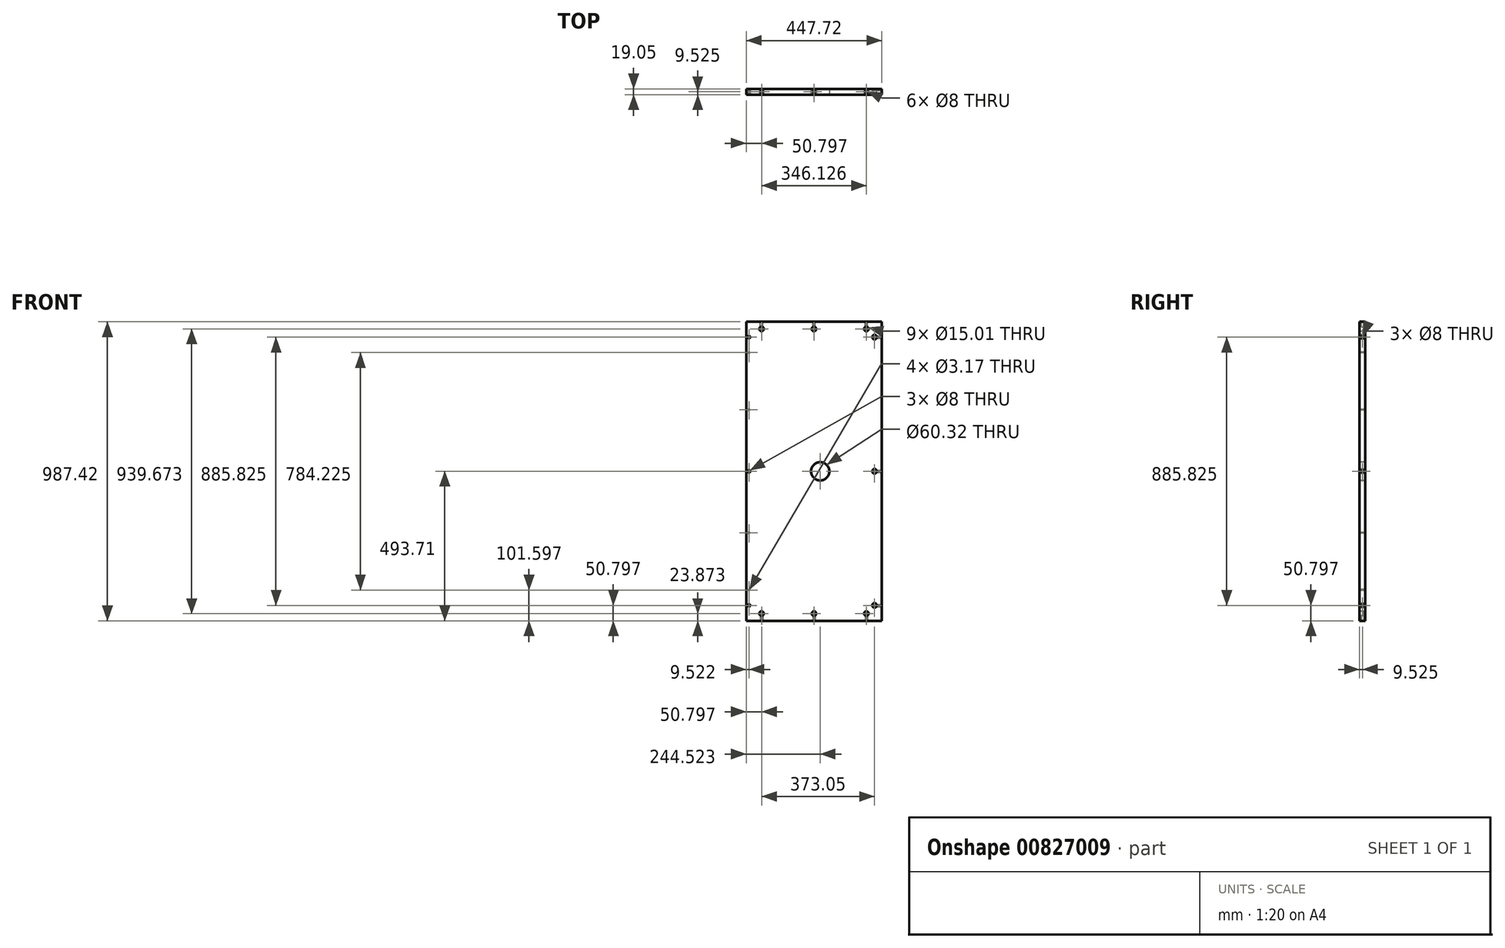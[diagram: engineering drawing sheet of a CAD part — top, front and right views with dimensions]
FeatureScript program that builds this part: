
annotation { "Feature Type Name" : "Feature", "Feature Type Description" : "" }
export const myFeature = defineFeature(function(context is Context, id is Id, definition is map)
    precondition{}
    {
        {
            var Q0;
            Q0=qCreatedBy(makeId("Front.planeOp"),FACE);
            var sketch = newSketch(context, id + "F0", { "sketchPlane" : qUnion([Q0])});
            skLineSegment(sketch, "E0.bottom", {"start": v(223.86, 493.71) * mm, "end": v(-223.86, 493.71) * mm});
            skLineSegment(sketch, "E0.top", {"start": v(223.86, -493.71) * mm, "end": v(-223.86, -493.71) * mm});
            skLineSegment(sketch, "E0.left", {"start": v(223.86, 493.71) * mm, "end": v(223.86, -493.71) * mm});
            skLineSegment(sketch, "E0.right", {"start": v(-223.86, 493.71) * mm, "end": v(-223.86, -493.71) * mm});
            skPoint(sketch, "E0.middle", {"position": v(0, 0) * mm});
            skSolve(sketch);
        }
        {
            var Q0;
            Q0=makeQuery(id+"F0.imprint","IMPRINT",FACE,{"disambiguationData":[TD([[makeQuery(id+"F0.imprint","IMPRINT",EDGE,{"derivedFrom":sQuery(id+"F0.wireOp",EDGE,"E0.bottom")}),1.0]])]});
            extrude(context, id + "F1", {"entities" : qUnion([Q0]), "depth" : 19.05 * mm, "offsetDistance" : 25.4 * mm});
        }
        {
            var Q0;
            Q0=makeQuery(id+"F1.opExtrude","CAP_FACE",FACE,{"disambiguationData":[OSD([sQuery(id+"F0.wireOp",EDGE,"E0.bottom"),sQuery(id+"F0.wireOp",EDGE,"E0.top"),sQuery(id+"F0.wireOp",EDGE,"E0.left"),sQuery(id+"F0.wireOp",EDGE,"E0.right")])],"isStart":false});
            var sketch = newSketch(context, id + "F2", { "sketchPlane" : qUnion([Q0])});
            skLineSegment(sketch, "E1", {"start": v(-223.86, 493.71) * mm, "end": v(-214.34, 493.71) * mm});
            skLineSegment(sketch, "E2", {"start": v(-214.34, 493.71) * mm, "end": v(-214.34, 442.91) * mm});
            skLineSegment(sketch, "E3", {"start": v(-223.86, -493.71) * mm, "end": v(-214.34, -493.71) * mm});
            skLineSegment(sketch, "E4", {"start": v(-214.34, -493.71) * mm, "end": v(-214.34, -442.91) * mm});
            skLineSegment(sketch, "E5", {"start": v(-223.86, 0) * mm, "end": v(-214.34, 0) * mm});
            skPoint(sketch, "E6", {"position": v(-214.34, 442.91) * mm});
            skPoint(sketch, "E7", {"position": v(-214.34, 0) * mm});
            skPoint(sketch, "E8", {"position": v(-214.34, -442.91) * mm});
            skLineSegment(sketch, "E9", {"start": v(-214.34, 442.91) * mm, "end": v(-214.34, 392.11) * mm});
            skLineSegment(sketch, "E10", {"start": v(-214.34, -442.91) * mm, "end": v(-214.34, -392.11) * mm});
            skLineSegment(sketch, "E11", {"start": v(-214.34, 0) * mm, "end": v(-214.34, -203.2) * mm});
            skLineSegment(sketch, "E12", {"start": v(-214.34, 0) * mm, "end": v(-214.34, 203.2) * mm});
            skSolve(sketch);
        }
        {
            var Q0;
            Q0=sQuery(id+"F2.wireOp",VERTEX,"E6");
            var Q1;
            Q1=sQuery(id+"F2.wireOp",VERTEX,"E7");
            var Q2;
            Q2=sQuery(id+"F2.wireOp",VERTEX,"E8");
            var Q3;
            Q3=makeQuery(id+"F1.opExtrude","SWEPT_BODY",BODY,{"disambiguationData":[OSD([sQuery(id+"F0.wireOp",EDGE,"E0.bottom"),sQuery(id+"F0.wireOp",EDGE,"E0.top"),sQuery(id+"F0.wireOp",EDGE,"E0.left"),sQuery(id+"F0.wireOp",EDGE,"E0.right")])]});
            hole(context, id + "F3", {"style" : HoleStyle.SIMPLE, "endStyle" : HoleEndStyle.BLIND, "holeDiameter" : 8 * mm, "majorDiameter" : 6.35 * mm, "holeDepth" : 25.4 * mm, "isTappedThrough" : true, "tappedDepth" : 12.7 * mm, "tapClearance" : 3, "startFromSketch" : true, "locations" : qUnion([Q0, Q1, Q2]), "scope" : qUnion([Q3])});
        }
        {
            var Q0;
            Q0=makeQuery(id+"F1.opExtrude","CAP_FACE",FACE,{"disambiguationData":[OSD([sQuery(id+"F0.wireOp",EDGE,"E0.bottom"),sQuery(id+"F0.wireOp",EDGE,"E0.top"),sQuery(id+"F0.wireOp",EDGE,"E0.left"),sQuery(id+"F0.wireOp",EDGE,"E0.right")])],"isStart":false});
            var sketch = newSketch(context, id + "F4", { "sketchPlane" : qUnion([Q0])});
            skLineSegment(sketch, "E13", {"start": v(-223.86, 493.71) * mm, "end": v(-173.06, 493.71) * mm});
            skLineSegment(sketch, "E14", {"start": v(-173.06, 493.71) * mm, "end": v(-173.06, 469.84) * mm});
            skLineSegment(sketch, "E15", {"start": v(223.86, 493.71) * mm, "end": v(173.06, 493.71) * mm});
            skLineSegment(sketch, "E16", {"start": v(173.06, 493.71) * mm, "end": v(173.06, 469.84) * mm});
            skLineSegment(sketch, "E17", {"start": v(0, 493.71) * mm, "end": v(0, 469.84) * mm});
            skLineSegment(sketch, "E18", {"start": v(-223.86, -493.71) * mm, "end": v(-173.06, -493.71) * mm});
            skLineSegment(sketch, "E19", {"start": v(-173.06, -493.71) * mm, "end": v(-173.06, -469.84) * mm});
            skLineSegment(sketch, "E20", {"start": v(223.86, -493.71) * mm, "end": v(173.06, -493.71) * mm});
            skLineSegment(sketch, "E21", {"start": v(173.06, -493.71) * mm, "end": v(173.06, -469.84) * mm});
            skLineSegment(sketch, "E22", {"start": v(0, -493.71) * mm, "end": v(0, -469.84) * mm});
            skLineSegment(sketch, "E23", {"start": v(223.86, 493.71) * mm, "end": v(223.86, 442.91) * mm});
            skLineSegment(sketch, "E24", {"start": v(223.86, 442.91) * mm, "end": v(199.99, 442.91) * mm});
            skLineSegment(sketch, "E25", {"start": v(223.86, -493.71) * mm, "end": v(223.86, -442.91) * mm});
            skLineSegment(sketch, "E26", {"start": v(223.86, -442.91) * mm, "end": v(199.99, -442.91) * mm});
            skLineSegment(sketch, "E27", {"start": v(223.86, 0) * mm, "end": v(199.99, 0) * mm});
            skLineSegment(sketch, "E28", {"start": v(223.86, 0) * mm, "end": v(20.66, 0) * mm});
            skCircle(sketch, "E29", {"center": v(20.66, 0) * mm, "radius": 30.16 * mm});
            skSolve(sketch);
        }
        {
            var Q0;
            Q0=makeQuery(id+"F4.imprint","IMPRINT",FACE,{"disambiguationData":[TD([[makeQuery(id+"F4.imprint","IMPRINT",EDGE,{"derivedFrom":sQuery(id+"F4.wireOp",EDGE,"E29")}),1.0]])]});
            extrude(context, id + "F5", {"entities" : qUnion([Q0]), "operationType" : NewBodyOperationType.REMOVE, "oppositeDirection" : true, "depth" : 25.4 * mm, "offsetDistance" : 25.4 * mm});
        }
        {
            var Q0;
            Q0=sQuery(id+"F4.wireOp",VERTEX,"E14.end");
            var Q1;
            Q1=sQuery(id+"F4.wireOp",VERTEX,"E17.end");
            var Q2;
            Q2=sQuery(id+"F4.wireOp",VERTEX,"E16.end");
            var Q3;
            Q3=sQuery(id+"F4.wireOp",VERTEX,"E24.end");
            var Q4;
            Q4=sQuery(id+"F4.wireOp",VERTEX,"E27.end");
            var Q5;
            Q5=sQuery(id+"F4.wireOp",VERTEX,"E26.end");
            var Q6;
            Q6=sQuery(id+"F4.wireOp",VERTEX,"E21.end");
            var Q7;
            Q7=sQuery(id+"F4.wireOp",VERTEX,"E22.end");
            var Q8;
            Q8=sQuery(id+"F4.wireOp",VERTEX,"E19.end");
            var Q9;
            Q9=makeQuery(id+"F1.opExtrude","SWEPT_BODY",BODY,{"disambiguationData":[OSD([sQuery(id+"F0.wireOp",EDGE,"E0.bottom"),sQuery(id+"F0.wireOp",EDGE,"E0.top"),sQuery(id+"F0.wireOp",EDGE,"E0.left"),sQuery(id+"F0.wireOp",EDGE,"E0.right")])]});
            hole(context, id + "F6", {"style" : HoleStyle.SIMPLE, "endStyle" : HoleEndStyle.BLIND, "holeDiameter" : 15 * mm, "majorDiameter" : 6.35 * mm, "holeDepth" : 14.22 * mm, "isTappedThrough" : true, "tappedDepth" : 12.7 * mm, "tapClearance" : 3, "startFromSketch" : true, "locations" : qUnion([Q0, Q1, Q2, Q3, Q4, Q5, Q6, Q7, Q8]), "scope" : qUnion([Q9])});
        }
        {
            var Q0;
            Q0=makeQuery(id+"F1.opExtrude","SWEPT_FACE",FACE,{"disambiguationData":[OSD([sQuery(id+"F0.wireOp",EDGE,"E0.top")])]});
            var sketch = newSketch(context, id + "F7", { "sketchPlane" : qUnion([Q0])});
            skLineSegment(sketch, "E30", {"start": v(-223.86, 9.53) * mm, "end": v(-173.06, 9.53) * mm});
            skLineSegment(sketch, "E31", {"start": v(223.86, 9.53) * mm, "end": v(173.06, 9.53) * mm});
            skLineSegment(sketch, "E32", {"start": v(0, 0) * mm, "end": v(0, 9.53) * mm});
            skSolve(sketch);
        }
        {
            var Q0;
            Q0=sQuery(id+"F7.wireOp",VERTEX,"E30.end");
            var Q1;
            Q1=sQuery(id+"F7.wireOp",VERTEX,"E32.end");
            var Q2;
            Q2=sQuery(id+"F7.wireOp",VERTEX,"E31.end");
            var Q3;
            Q3=makeQuery(id+"F1.opExtrude","SWEPT_BODY",BODY,{"disambiguationData":[OSD([sQuery(id+"F0.wireOp",EDGE,"E0.bottom"),sQuery(id+"F0.wireOp",EDGE,"E0.top"),sQuery(id+"F0.wireOp",EDGE,"E0.left"),sQuery(id+"F0.wireOp",EDGE,"E0.right")])]});
            hole(context, id + "F8", {"style" : HoleStyle.SIMPLE, "endStyle" : HoleEndStyle.BLIND, "holeDiameter" : 8 * mm, "majorDiameter" : 6.35 * mm, "holeDepth" : 25.4 * mm, "isTappedThrough" : true, "tappedDepth" : 12.7 * mm, "tapClearance" : 3, "startFromSketch" : true, "locations" : qUnion([Q0, Q1, Q2]), "scope" : qUnion([Q3])});
        }
        {
            var Q0;
            Q0=makeQuery(id+"F1.opExtrude","SWEPT_FACE",FACE,{"disambiguationData":[OSD([sQuery(id+"F0.wireOp",EDGE,"E0.bottom")])]});
            var sketch = newSketch(context, id + "F9", { "sketchPlane" : qUnion([Q0])});
            skLineSegment(sketch, "E33", {"start": v(-223.86, -9.53) * mm, "end": v(-173.06, -9.53) * mm});
            skLineSegment(sketch, "E34", {"start": v(223.86, -9.53) * mm, "end": v(173.06, -9.53) * mm});
            skLineSegment(sketch, "E35", {"start": v(0, 0) * mm, "end": v(0, -9.53) * mm});
            skSolve(sketch);
        }
        {
            var Q0;
            Q0=sQuery(id+"F9.wireOp",VERTEX,"E33.end");
            var Q1;
            Q1=sQuery(id+"F9.wireOp",VERTEX,"E35.end");
            var Q2;
            Q2=sQuery(id+"F9.wireOp",VERTEX,"E34.end");
            var Q3;
            Q3=makeQuery(id+"F1.opExtrude","SWEPT_BODY",BODY,{"disambiguationData":[OSD([sQuery(id+"F0.wireOp",EDGE,"E0.bottom"),sQuery(id+"F0.wireOp",EDGE,"E0.top"),sQuery(id+"F0.wireOp",EDGE,"E0.left"),sQuery(id+"F0.wireOp",EDGE,"E0.right")])]});
            hole(context, id + "F10", {"style" : HoleStyle.SIMPLE, "endStyle" : HoleEndStyle.BLIND, "holeDiameter" : 8 * mm, "majorDiameter" : 6.35 * mm, "holeDepth" : 25.4 * mm, "isTappedThrough" : true, "tappedDepth" : 12.7 * mm, "tapClearance" : 3, "startFromSketch" : true, "locations" : qUnion([Q0, Q1, Q2]), "scope" : qUnion([Q3])});
        }
        {
            var Q0;
            Q0=makeQuery(id+"F1.opExtrude","SWEPT_FACE",FACE,{"disambiguationData":[OSD([sQuery(id+"F0.wireOp",EDGE,"E0.left")])]});
            var sketch = newSketch(context, id + "F11", { "sketchPlane" : qUnion([Q0])});
            skLineSegment(sketch, "E36", {"start": v(-9.53, 493.71) * mm, "end": v(-9.53, 442.91) * mm});
            skLineSegment(sketch, "E37", {"start": v(-9.53, -493.71) * mm, "end": v(-9.53, -442.91) * mm});
            skLineSegment(sketch, "E38", {"start": v(0, 0) * mm, "end": v(-9.53, 0) * mm});
            skSolve(sketch);
        }
        {
            var Q0;
            Q0=sQuery(id+"F11.wireOp",VERTEX,"E38.end");
            var Q1;
            Q1=sQuery(id+"F11.wireOp",VERTEX,"E37.end");
            var Q2;
            Q2=sQuery(id+"F11.wireOp",VERTEX,"E36.end");
            var Q3;
            Q3=makeQuery(id+"F1.opExtrude","SWEPT_BODY",BODY,{"disambiguationData":[OSD([sQuery(id+"F0.wireOp",EDGE,"E0.bottom"),sQuery(id+"F0.wireOp",EDGE,"E0.top"),sQuery(id+"F0.wireOp",EDGE,"E0.left"),sQuery(id+"F0.wireOp",EDGE,"E0.right")])]});
            hole(context, id + "F12", {"style" : HoleStyle.SIMPLE, "endStyle" : HoleEndStyle.BLIND, "holeDiameter" : 8 * mm, "majorDiameter" : 6.35 * mm, "holeDepth" : 25.4 * mm, "isTappedThrough" : true, "tappedDepth" : 12.7 * mm, "tapClearance" : 3, "startFromSketch" : true, "locations" : qUnion([Q0, Q1, Q2]), "scope" : qUnion([Q3])});
        }
        {
            var Q0;
            Q0=sQuery(id+"F2.wireOp",VERTEX,"E9.end");
            var Q1;
            Q1=sQuery(id+"F2.wireOp",VERTEX,"E12.end");
            var Q2;
            Q2=sQuery(id+"F2.wireOp",VERTEX,"E11.end");
            var Q3;
            Q3=sQuery(id+"F2.wireOp",VERTEX,"E10.end");
            var Q4;
            Q4=makeQuery(id+"F1.opExtrude","SWEPT_BODY",BODY,{"disambiguationData":[OSD([sQuery(id+"F0.wireOp",EDGE,"E0.bottom"),sQuery(id+"F0.wireOp",EDGE,"E0.top"),sQuery(id+"F0.wireOp",EDGE,"E0.left"),sQuery(id+"F0.wireOp",EDGE,"E0.right")])]});
            hole(context, id + "F13", {"style" : HoleStyle.SIMPLE, "endStyle" : HoleEndStyle.BLIND, "holeDiameter" : 3.17 * mm, "majorDiameter" : 6.35 * mm, "holeDepth" : 25.4 * mm, "isTappedThrough" : true, "tappedDepth" : 12.7 * mm, "tapClearance" : 3, "startFromSketch" : true, "locations" : qUnion([Q0, Q1, Q2, Q3]), "scope" : qUnion([Q4])});
        }
    });
